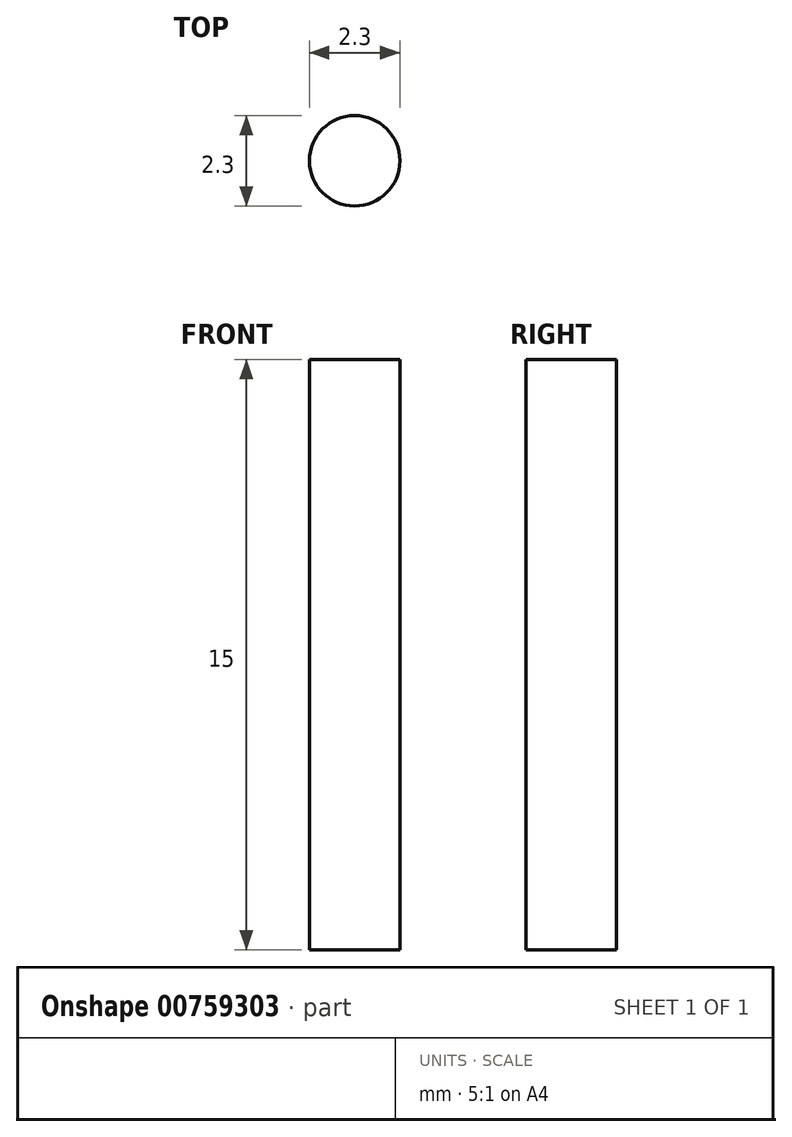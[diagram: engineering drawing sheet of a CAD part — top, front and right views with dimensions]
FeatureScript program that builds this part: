
annotation { "Feature Type Name" : "Feature", "Feature Type Description" : "" }
export const myFeature = defineFeature(function(context is Context, id is Id, definition is map)
    precondition{}
    {
        {
            var Q0;
            Q0=qCreatedBy(makeId("Top.planeOp"),FACE);
            var sketch = newSketch(context, id + "F0", { "sketchPlane" : qUnion([Q0])});
            skCircle(sketch, "E0", {"center": v(0, 0) * mm, "radius": 1.15 * mm});
            skSolve(sketch);
        }
        {
            var Q0;
            Q0=qCreatedBy(makeId("Top.planeOp"),FACE);
            var sketch = newSketch(context, id + "F1", { "sketchPlane" : qUnion([Q0])});
            skSolve(sketch);
        }
        {
            var Q0;
            Q0 = qSketchRegion(id + "F1", true);
            var Q1;
            Q1=makeQuery(id+"F0.imprint","IMPRINT",FACE,{"disambiguationData":[TD([[makeQuery(id+"F0.imprint","IMPRINT",EDGE,{"derivedFrom":sQuery(id+"F0.wireOp",EDGE,"E0")}),1.0]])]});
            extrude(context, id + "F2", {"entities" : qUnion([Q0, Q1]), "depth" : 15 * mm, "offsetDistance" : 25 * mm});
        }
    });
